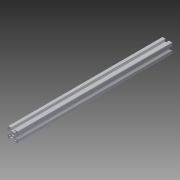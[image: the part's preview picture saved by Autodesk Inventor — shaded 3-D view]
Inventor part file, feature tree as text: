
AUTODESK INVENTOR PART (.ipt)
format: ipt  version: 2013 (Build 170138000, 138)  size: 325,120 bytes
history: native  units: in
note: dims shown in document units (in); Inventor stores cm internally (conversion verified against a paired STEP export)
features: other x3, extrude x2, sketch x2
ambient origin geometry x8: Origin, YZ Plane, XZ Plane, XY Plane, X Axis, Y Axis, Z Axis, Center Point
bodies: Solid1 (feature_tree)
feature tree (7):
  other  "Blocks"
  extrude  "Extrusion1"  Depth=0.25in
  extrude  "Extrusion2"  [1 undecoded]
  sketch  "Sketch1"  dims[d1=0.0in d2=0.25in]
  other  "20x20"
  sketch  "Sketch2"  dims[d3=0.3125in d4=0.0in]
  other  "20x20:1"
note: 1 required parameter value undecoded (feature->parameter linkage not recoverable at this tier; creation-order binding heuristic only, values carry confidence <= 0.55)
